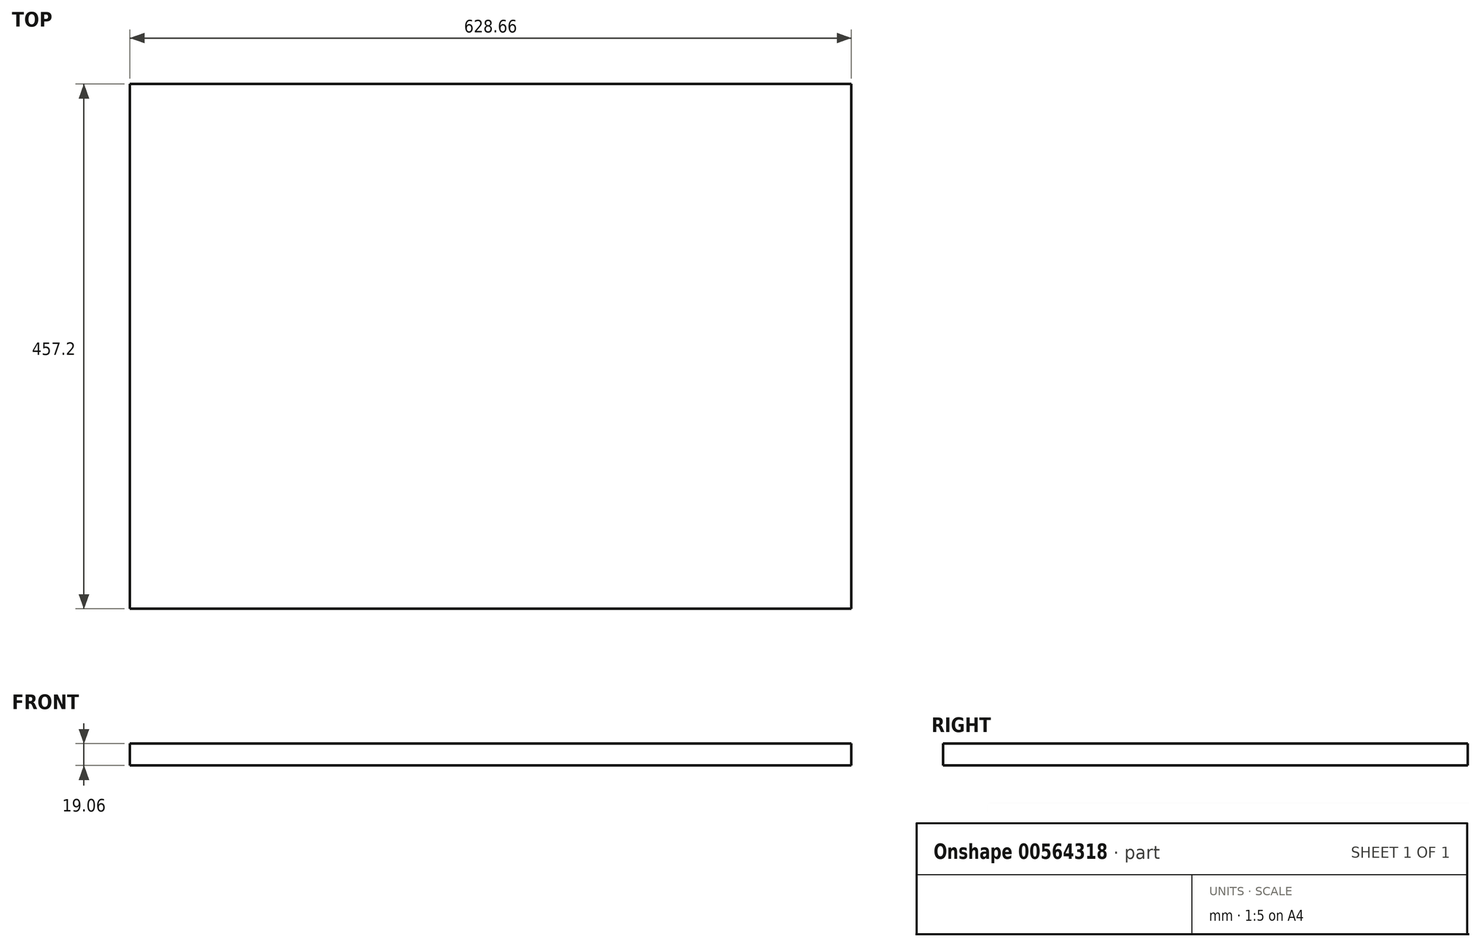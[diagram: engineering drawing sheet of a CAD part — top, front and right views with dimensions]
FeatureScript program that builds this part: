
annotation { "Feature Type Name" : "Feature", "Feature Type Description" : "" }
export const myFeature = defineFeature(function(context is Context, id is Id, definition is map)
    precondition{}
    {
        {
            var Q0;
            Q0=qCreatedBy(makeId("Front.planeOp"),FACE);
            var sketch = newSketch(context, id + "F0", { "sketchPlane" : qUnion([Q0])});
            skLineSegment(sketch, "E0.bottom", {"start": v(-314.32, 9.53) * mm, "end": v(314.33, 9.53) * mm});
            skLineSegment(sketch, "E0.top", {"start": v(-314.32, -9.53) * mm, "end": v(314.33, -9.53) * mm});
            skLineSegment(sketch, "E0.left", {"start": v(-314.33, 9.53) * mm, "end": v(-314.33, -9.53) * mm});
            skLineSegment(sketch, "E0.right", {"start": v(314.33, 9.53) * mm, "end": v(314.33, -9.53) * mm});
            skPoint(sketch, "E0.middle", {"position": v(0, 0) * mm});
            skSolve(sketch);
        }
        {
            var Q0;
            Q0 = qSketchRegion(id + "F0", true);
            extrude(context, id + "F1", {"entities" : qUnion([Q0]), "depth" : 457.2 * mm, "offsetDistance" : 25.4 * mm});
        }
    });
